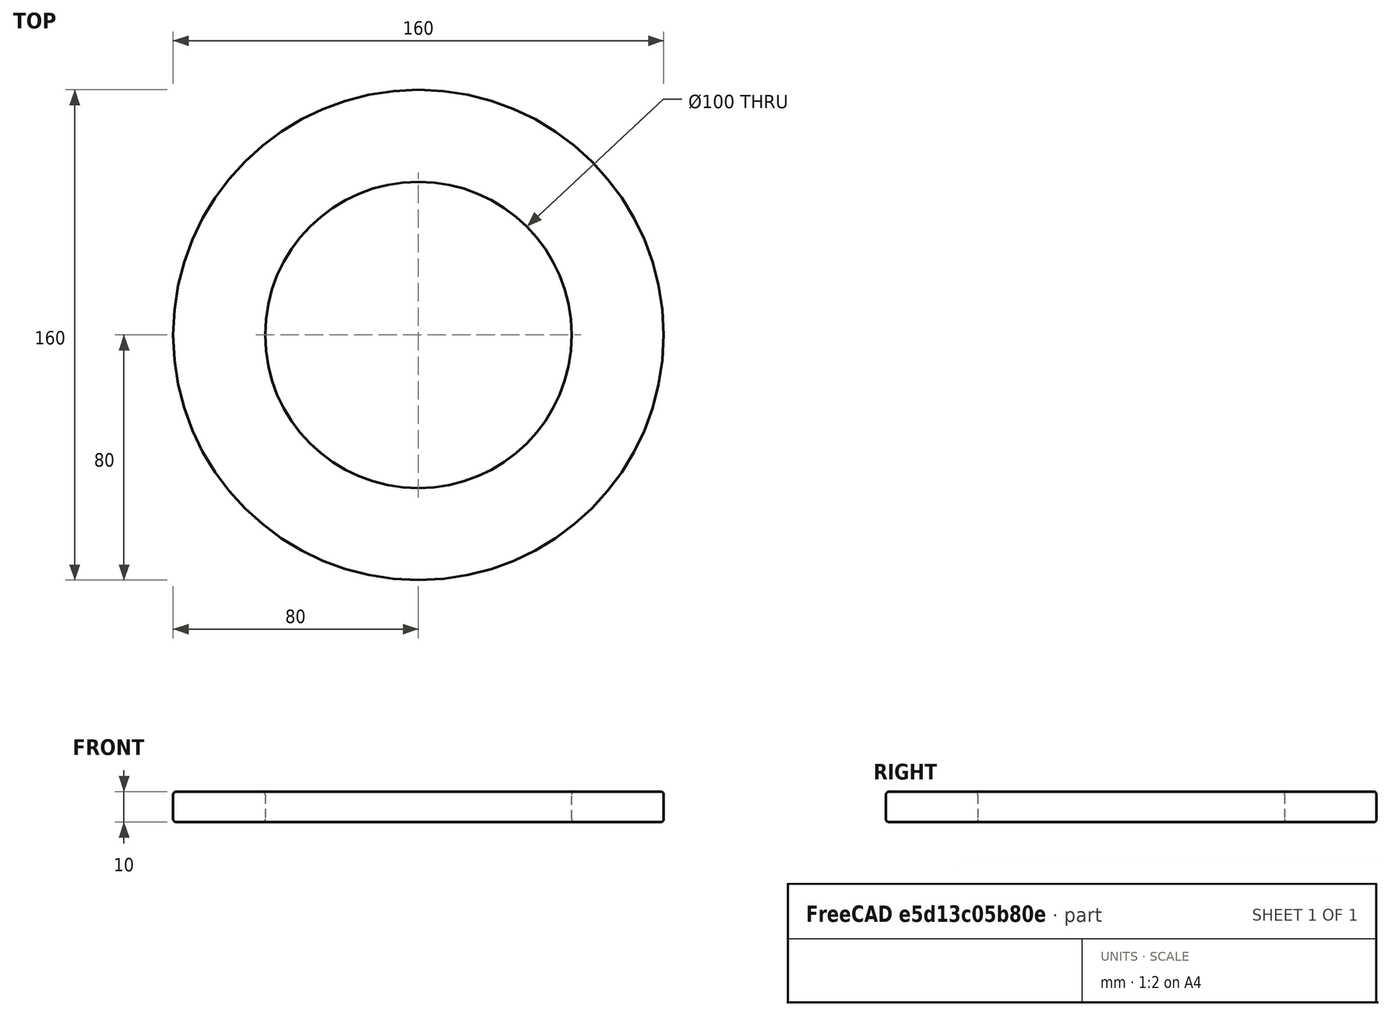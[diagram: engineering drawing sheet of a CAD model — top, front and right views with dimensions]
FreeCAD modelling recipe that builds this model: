
FCSTD DOCUMENT  (FreeCAD 0.18.3R)
Label: lager
License: All rights reserved
LicenseURL: http://en.wikipedia.org/wiki/All_rights_reserved
objects: Sketcher::SketchObject×1, PartDesign::Pad×1, PartDesign::Fillet×1, PartDesign::Body×1
note: 5 computed .brp shape members not serialized (recipe doc carries the construction recipe); baked Part::Feature solids carry a one-line shape summary decoded from their .brp

FEATURE [Sketcher::SketchObject] Sketch001
  MapMode = 5
  Support = -> [XY_Plane001]
  sketch-geometry (2):
    g0: Circle CenterX=0 CenterY=0 CenterZ=0 NormalX=0 NormalY=0 NormalZ=1 AngleXU=0 Radius=50
    g1: Circle CenterX=0 CenterY=0 CenterZ=0 NormalX=0 NormalY=0 NormalZ=1 AngleXU=0 Radius=80
  constraints (4):
    c: Coincident(g1,g-1)
    c: Coincident(g0,g1)
    c: Radius(g0) = 50
    c: Radius(g1) = 80
FEATURE [PartDesign::Pad] Pad001
  Length = 10
  Length2 = 100
  Profile = -> Sketch001
  Type = 0
FEATURE [PartDesign::Fillet] Fillet001
  Base = -> Pad001 [Edge3,Edge2,Edge6,Edge5]
  BaseFeature = -> Pad001
  Radius = 1
FEATURE [PartDesign::Body] Body001  label="Lager002"
  Group = -> [Sketch001,Pad001,Fillet001]
  Origin = -> Origin001
  Placement = pos=(0,0,-59) rot=(0,0,1;0rad)
  Tip = -> Fillet001
